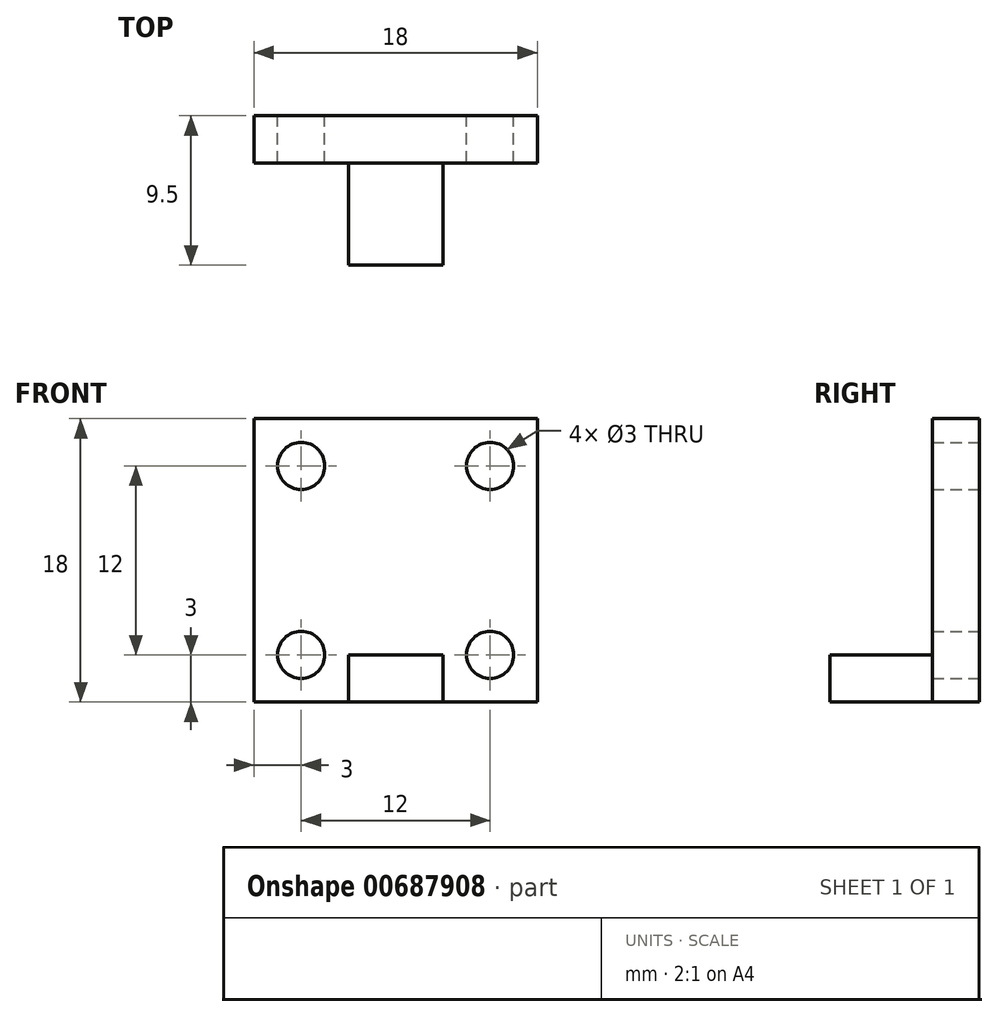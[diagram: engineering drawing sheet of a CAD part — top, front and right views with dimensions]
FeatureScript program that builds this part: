
annotation { "Feature Type Name" : "Feature", "Feature Type Description" : "" }
export const myFeature = defineFeature(function(context is Context, id is Id, definition is map)
    precondition{}
    {
        {
            var Q0;
            Q0=qCreatedBy(makeId("Front.planeOp"),FACE);
            var sketch = newSketch(context, id + "F0", { "sketchPlane" : qUnion([Q0])});
            skLineSegment(sketch, "E0.bottom", {"start": v(-9, 9) * mm, "end": v(9, 9) * mm});
            skLineSegment(sketch, "E0.top", {"start": v(-9, -9) * mm, "end": v(9, -9) * mm});
            skLineSegment(sketch, "E0.left", {"start": v(-9, 9) * mm, "end": v(-9, -9) * mm});
            skLineSegment(sketch, "E0.right", {"start": v(9, 9) * mm, "end": v(9, -9) * mm});
            skLineSegment(sketch, "E1.bottom", {"start": v(-6, 6) * mm, "end": v(6, 6) * mm, "construction": true});
            skLineSegment(sketch, "E1.top", {"start": v(-6, -6) * mm, "end": v(6, -6) * mm, "construction": true});
            skLineSegment(sketch, "E1.left", {"start": v(-6, 6) * mm, "end": v(-6, -6) * mm, "construction": true});
            skLineSegment(sketch, "E1.right", {"start": v(6, 6) * mm, "end": v(6, -6) * mm, "construction": true});
            skCircle(sketch, "E2", {"center": v(-6, 6) * mm, "radius": 1.5 * mm});
            skCircle(sketch, "E3", {"center": v(6, 6) * mm, "radius": 1.5 * mm});
            skCircle(sketch, "E4", {"center": v(6, -6) * mm, "radius": 1.5 * mm});
            skCircle(sketch, "E5", {"center": v(-6, -6) * mm, "radius": 1.5 * mm});
            skSolve(sketch);
        }
        {
            var Q0;
            Q0 = qSketchRegion(id + "F0", true);
            extrude(context, id + "F1", {"entities" : qUnion([Q0]), "depth" : 3 * mm, "offsetDistance" : 25 * mm});
        }
        {
            var Q0;
            Q0=makeQuery(id+"F1.opExtrude","CAP_FACE",FACE,{"disambiguationData":[OSD([sQuery(id+"F0.wireOp",EDGE,"E0.bottom"),sQuery(id+"F0.wireOp",EDGE,"E0.top"),sQuery(id+"F0.wireOp",EDGE,"E0.left"),sQuery(id+"F0.wireOp",EDGE,"E0.right"),sQuery(id+"F0.wireOp",EDGE,"E2"),sQuery(id+"F0.wireOp",EDGE,"E3"),sQuery(id+"F0.wireOp",EDGE,"E4"),sQuery(id+"F0.wireOp",EDGE,"E5")])],"isStart":false});
            var sketch = newSketch(context, id + "F2", { "sketchPlane" : qUnion([Q0])});
            skLineSegment(sketch, "E6.bottom", {"start": v(-3, -9) * mm, "end": v(3, -9) * mm});
            skLineSegment(sketch, "E6.top", {"start": v(-3, -6) * mm, "end": v(3, -6) * mm});
            skLineSegment(sketch, "E6.left", {"start": v(-3, -9) * mm, "end": v(-3, -6) * mm});
            skLineSegment(sketch, "E6.right", {"start": v(3, -9) * mm, "end": v(3, -6) * mm});
            skSolve(sketch);
        }
        {
            var Q0;
            Q0 = qSketchRegion(id + "F2", true);
            extrude(context, id + "F3", {"entities" : qUnion([Q0]), "operationType" : NewBodyOperationType.ADD, "depth" : 6.5 * mm, "offsetDistance" : 25 * mm});
        }
    });
